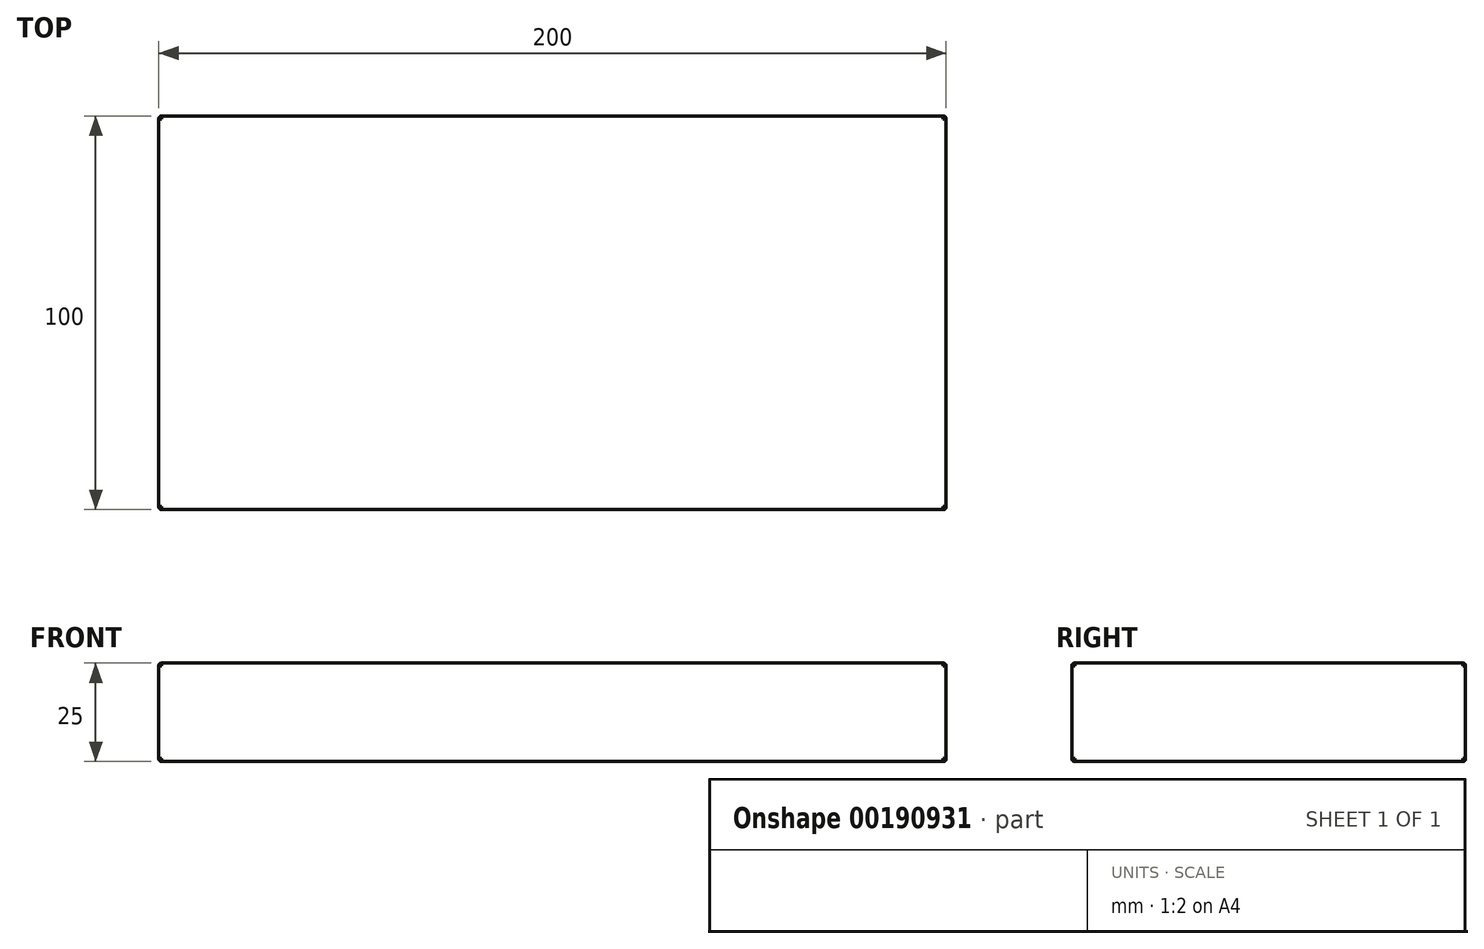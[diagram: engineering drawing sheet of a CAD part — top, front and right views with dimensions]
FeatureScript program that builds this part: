
annotation { "Feature Type Name" : "Feature", "Feature Type Description" : "" }
export const myFeature = defineFeature(function(context is Context, id is Id, definition is map)
    precondition{}
    {
        {
            var Q0;
            Q0=qCreatedBy(makeId("Top.planeOp"),FACE);
            var sketch = newSketch(context, id + "F0", { "sketchPlane" : qUnion([Q0])});
            skLineSegment(sketch, "E0.bottom", {"start": v(100, 50) * mm, "end": v(-100, 50) * mm});
            skLineSegment(sketch, "E0.top", {"start": v(100, -50) * mm, "end": v(-100, -50) * mm});
            skLineSegment(sketch, "E0.left", {"start": v(100, 50) * mm, "end": v(100, -50) * mm});
            skLineSegment(sketch, "E0.right", {"start": v(-100, 50) * mm, "end": v(-100, -50) * mm});
            skPoint(sketch, "E0.middle", {"position": v(0, 0) * mm});
            skSolve(sketch);
        }
        {
            var Q0;
            Q0 = qSketchRegion(id + "F0", true);
            extrude(context, id + "F1", {"entities" : qUnion([Q0]), "depth" : 25 * mm, "offsetDistance" : 25 * mm, "symmetric" : true});
        }
        {
            var Q0;
            Q0=makeQuery(id+"F1.opExtrude","CAP_FACE",FACE,{"disambiguationData":[OSD([sQuery(id+"F0.wireOp",EDGE,"E0.bottom"),sQuery(id+"F0.wireOp",EDGE,"E0.top"),sQuery(id+"F0.wireOp",EDGE,"E0.left"),sQuery(id+"F0.wireOp",EDGE,"E0.right")])],"isStart":false});
            var Q1;
            Q1=makeQuery(id+"F1.opExtrude","CAP_FACE",FACE,{"disambiguationData":[OSD([sQuery(id+"F0.wireOp",EDGE,"E0.bottom"),sQuery(id+"F0.wireOp",EDGE,"E0.top"),sQuery(id+"F0.wireOp",EDGE,"E0.left"),sQuery(id+"F0.wireOp",EDGE,"E0.right")])],"isStart":true});
            var Q2;
            Q2=makeQuery(id+"F1.opExtrude","SWEPT_FACE",FACE,{"disambiguationData":[OSD([sQuery(id+"F0.wireOp",EDGE,"E0.top")])]});
            var Q3;
            Q3=makeQuery(id+"F1.opExtrude","SWEPT_FACE",FACE,{"disambiguationData":[OSD([sQuery(id+"F0.wireOp",EDGE,"E0.bottom")])]});
            fillet(context, id + "F2", {"entities" : qUnion([Q0, Q1, Q2, Q3]), "radius" : 0.75 * mm, "tangentPropagation" : true, "rho" : 0.5, "crossSection" : FilletCrossSection.CONIC, "allowEdgeOverflow" : false});
        }
    });
